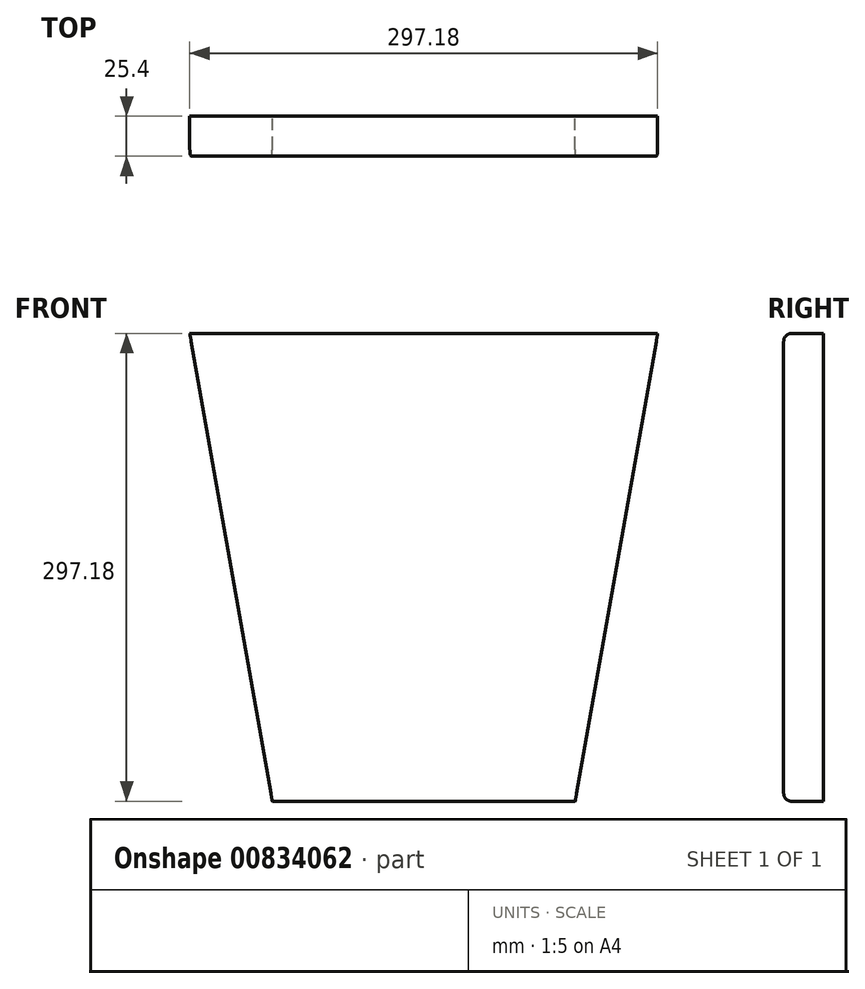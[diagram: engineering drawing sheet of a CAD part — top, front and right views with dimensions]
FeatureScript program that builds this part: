
annotation { "Feature Type Name" : "Feature", "Feature Type Description" : "" }
export const myFeature = defineFeature(function(context is Context, id is Id, definition is map)
    precondition{}
    {
        {
            var Q0;
            Q0=qCreatedBy(makeId("Front.planeOp"),FACE);
            var sketch = newSketch(context, id + "F0", { "sketchPlane" : qUnion([Q0])});
            skLineSegment(sketch, "E0", {"start": v(-126.82, 545.53) * mm, "end": v(170.36, 545.53) * mm});
            skLineSegment(sketch, "E1", {"start": v(-126.82, 545.53) * mm, "end": v(-91, 342.4) * mm});
            skLineSegment(sketch, "E2", {"start": v(170.36, 545.53) * mm, "end": v(125.07, 288.66) * mm});
            skLineSegment(sketch, "E3", {"start": v(21.77, 248.35) * mm, "end": v(117.96, 248.35) * mm});
            skLineSegment(sketch, "E4", {"start": v(-91, 342.4) * mm, "end": v(-74.42, 248.35) * mm});
            skLineSegment(sketch, "E5", {"start": v(125.07, 288.66) * mm, "end": v(117.96, 248.35) * mm});
            skLineSegment(sketch, "E6", {"start": v(21.77, 248.35) * mm, "end": v(21.77, 545.53) * mm});
            skLineSegment(sketch, "E7", {"start": v(-74.42, 248.35) * mm, "end": v(21.77, 248.35) * mm});
            skSolve(sketch);
        }
        {
            var Q0;
            Q0 = qSketchRegion(id + "F0", true);
            extrude(context, id + "F1", {"entities" : qUnion([Q0]), "depth" : 25.4 * mm, "offsetDistance" : 25.4 * mm});
        }
        {
            var Q0;
            Q0=makeQuery(id+"F1.opExtrude","CAP_EDGE",EDGE,{"disambiguationData":[OSD([sQuery(id+"F0.wireOp",EDGE,"E3"),sQuery(id+"F0.wireOp",EDGE,"E7")])],"isStart":false});
            var Q1;
            Q1=makeQuery(id+"F1.opExtrude","CAP_EDGE",EDGE,{"disambiguationData":[OSD([sQuery(id+"F0.wireOp",EDGE,"E0")])],"isStart":false});
            fillet(context, id + "F2", {"entities" : qUnion([Q0, Q1]), "radius" : 5.08 * mm, "tangentPropagation" : true, "allowEdgeOverflow" : false});
        }
    });
